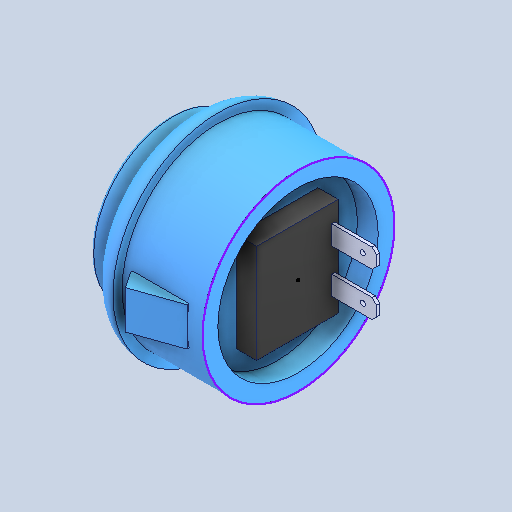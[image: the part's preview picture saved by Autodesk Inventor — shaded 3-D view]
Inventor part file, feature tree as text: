
AUTODESK INVENTOR PART (.ipt)
format: ipt  version: 2023.4 (Build 274418000, 418)  size: 363,520 bytes
history: native  units: in
note: dims shown in document units (in); Inventor stores cm internally (conversion verified against a paired STEP export)
features: sketch x1, fillet x1
ambient origin geometry x8: Origin, YZ Plane, XZ Plane, XY Plane, X Axis, Y Axis, Z Axis, Center Point
bodies: Solid1 (feature_tree)
feature tree (2):
  sketch  "Sketch1"
  fillet  "Fillet1"  [1 undecoded]
note: 1 required parameter value undecoded (feature->parameter linkage not recoverable at this tier; creation-order binding heuristic only, values carry confidence <= 0.55)
